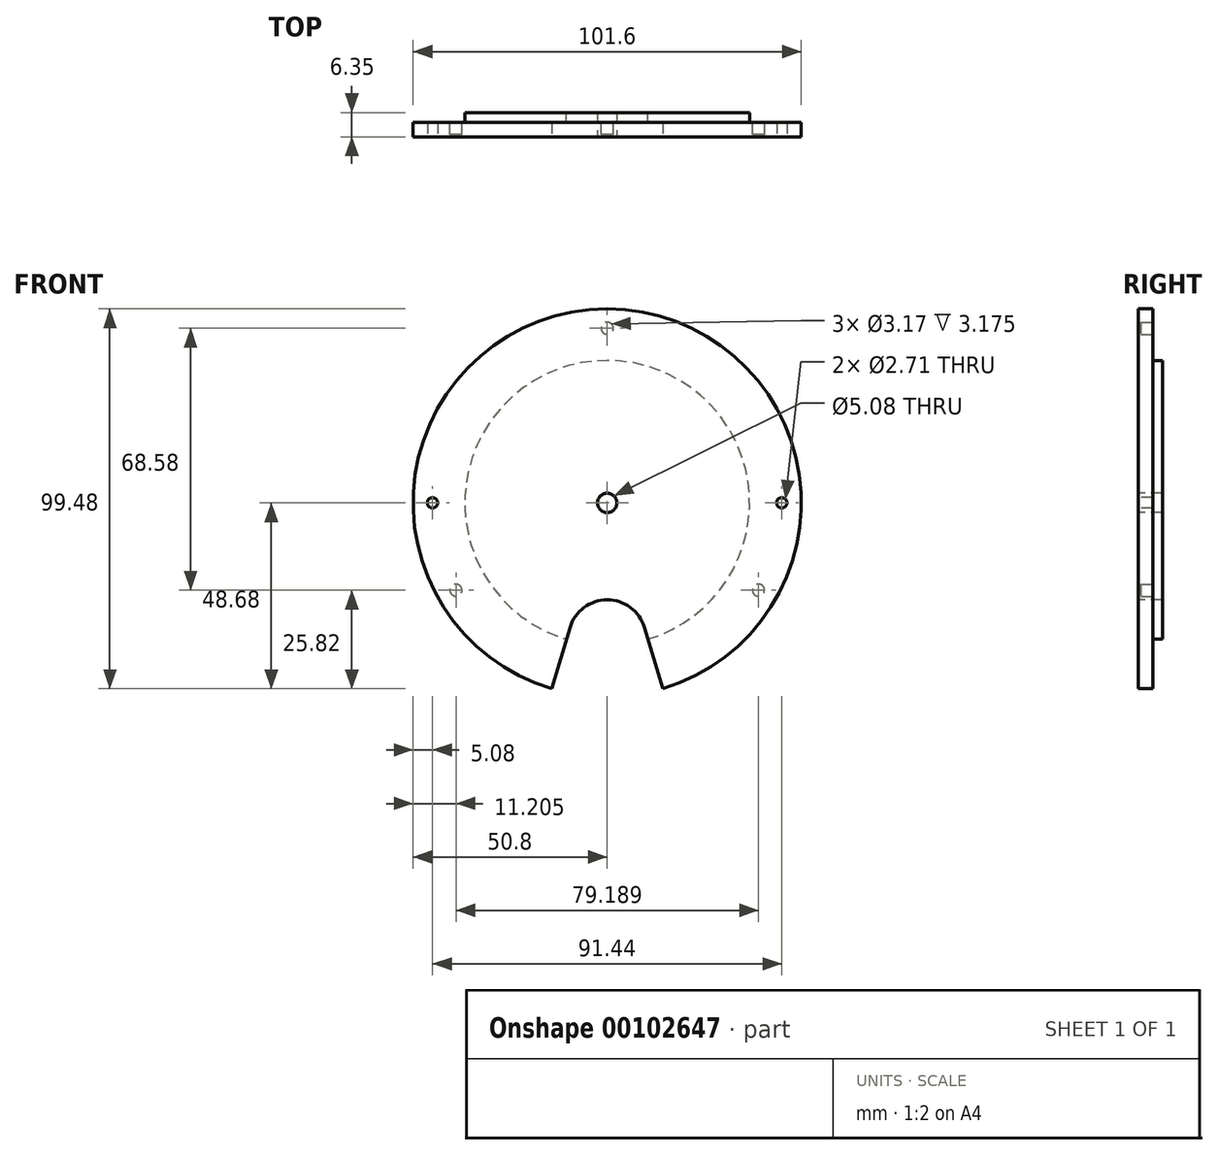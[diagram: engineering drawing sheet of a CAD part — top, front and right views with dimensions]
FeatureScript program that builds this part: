
annotation { "Feature Type Name" : "Feature", "Feature Type Description" : "" }
export const myFeature = defineFeature(function(context is Context, id is Id, definition is map)
    precondition{}
    {
        {
            var Q0;
            Q0=qCreatedBy(makeId("Front.planeOp"),FACE);
            var sketch = newSketch(context, id + "F0", { "sketchPlane" : qUnion([Q0])});
            skCircle(sketch, "E0", {"center": v(0, 0) * mm, "radius": 50.8 * mm});
            skSolve(sketch);
        }
        {
            var Q0;
            Q0=makeQuery(id+"F0.imprint","IMPRINT",FACE,{"disambiguationData":[TD([[makeQuery(id+"F0.imprint","IMPRINT",EDGE,{"derivedFrom":sQuery(id+"F0.wireOp",EDGE,"E0")}),1.0]])]});
            extrude(context, id + "F1", {"entities" : qUnion([Q0]), "oppositeDirection" : true, "depth" : 6.35 * mm});
        }
        {
            var Q0;
            Q0=makeQuery(id+"F1.opExtrude","CAP_FACE",FACE,{"disambiguationData":[OSD([sQuery(id+"F0.wireOp",EDGE,"E0")])],"isStart":false});
            var sketch = newSketch(context, id + "F2", { "sketchPlane" : qUnion([Q0])});
            skCircle(sketch, "E1", {"center": v(0, 0) * mm, "radius": 37.27 * mm});
            skSolve(sketch);
        }
        {
            var Q0;
            Q0=makeQuery(id+"F2.imprint","IMPRINT",FACE,{"disambiguationData":[TD([[makeQuery(id+"F2.imprint","IMPRINT",EDGE,{"derivedFrom":sQuery(id+"F2.wireOp",EDGE,"E1")}),-1.0]])]});
            extrude(context, id + "F3", {"entities" : qUnion([Q0]), "operationType" : NewBodyOperationType.REMOVE, "oppositeDirection" : true, "depth" : 2.54 * mm});
        }
        {
            var Q0;
            Q0=makeQuery(id+"F1.opExtrude","CAP_FACE",FACE,{"disambiguationData":[OSD([sQuery(id+"F0.wireOp",EDGE,"E0")])],"isStart":true});
            var sketch = newSketch(context, id + "F4", { "sketchPlane" : qUnion([Q0])});
            skCircle(sketch, "E2", {"center": v(0, 0) * mm, "radius": 2.54 * mm});
            skLineSegment(sketch, "E3", {"start": v(0, 63.69) * mm, "end": v(0, -59.89) * mm, "construction": true});
            skLineSegment(sketch, "E4", {"start": v(-63.21, 0) * mm, "end": v(63.78, 0) * mm, "construction": true});
            skCircle(sketch, "E5", {"center": v(-45.72, 0) * mm, "radius": 1.35 * mm});
            skCircle(sketch, "E6", {"center": v(45.72, 0) * mm, "radius": 1.35 * mm});
            skSolve(sketch);
        }
        {
            var Q0;
            Q0=makeQuery(id+"F4.imprint","IMPRINT",FACE,{"disambiguationData":[TD([[makeQuery(id+"F4.imprint","IMPRINT",EDGE,{"derivedFrom":sQuery(id+"F4.wireOp",EDGE,"E2")}),1.0]])]});
            var Q1;
            Q1=makeQuery(id+"F4.imprint","IMPRINT",FACE,{"disambiguationData":[TD([[makeQuery(id+"F4.imprint","IMPRINT",EDGE,{"derivedFrom":sQuery(id+"F4.wireOp",EDGE,"E5")}),1.0]])]});
            var Q2;
            Q2=makeQuery(id+"F4.imprint","IMPRINT",FACE,{"disambiguationData":[TD([[makeQuery(id+"F4.imprint","IMPRINT",EDGE,{"derivedFrom":sQuery(id+"F4.wireOp",EDGE,"E6")}),1.0]])]});
            extrude(context, id + "F5", {"entities" : qUnion([Q0, Q1, Q2]), "operationType" : NewBodyOperationType.REMOVE, "endBound" : BoundingType.THROUGH_ALL, "oppositeDirection" : true, "depth" : 25 * mm});
        }
        {
            var Q0;
            Q0=makeQuery(id+"F1.opExtrude","CAP_FACE",FACE,{"disambiguationData":[OSD([sQuery(id+"F0.wireOp",EDGE,"E0")])],"isStart":true});
            var sketch = newSketch(context, id + "F6", { "sketchPlane" : qUnion([Q0])});
            skLineSegment(sketch, "E7", {"start": v(0, 39.75) * mm, "end": v(0, -44.83) * mm, "construction": true});
            skCircle(sketch, "E8", {"center": v(0, 0) * mm, "radius": 25.4 * mm, "construction": true});
            skCircle(sketch, "E9", {"center": v(0, -35.56) * mm, "radius": 10.16 * mm, "construction": true});
            skPoint(sketch, "E9.first.point", {"position": v(0, -25.4) * mm});
            skPoint(sketch, "E9.second.point", {"position": v(-10.15, -35.13) * mm});
            skPoint(sketch, "E9.third.point", {"position": v(10.15, -35.2) * mm});
            skLineSegment(sketch, "E10", {"start": v(0, 0) * mm, "end": v(-14.51, -48.68) * mm, "construction": true});
            skLineSegment(sketch, "E11", {"start": v(0, 0) * mm, "end": v(14.51, -48.68) * mm, "construction": true});
            skLineSegment(sketch, "E12", {"start": v(-9.74, -32.66) * mm, "end": v(-14.51, -48.68) * mm});
            skLineSegment(sketch, "E13", {"start": v(9.74, -32.66) * mm, "end": v(14.51, -48.68) * mm});
            skArc(sketch, "E14", {"start": v(-9.74, -32.66) * mm, "mid": v(0, -25.4) * mm, "end": v(9.74, -32.66) * mm});
            skSolve(sketch);
        }
        {
            var Q0;
            Q0 = qSketchRegion(id + "F6", true);
            var Q1;
            {var subQ0=sQuery(id+"F6.wireOp",EDGE,"E12");Q1=makeQuery(id+"F6.imprint","IMPRINT",FACE,{"disambiguationData":[TD([[makeQuery(id+"F6.imprint","IMPRINT",EDGE,{"derivedFrom":subQ0}),1.0]])]});}
            extrude(context, id + "F7", {"entities" : qUnion([Q0, Q1]), "operationType" : NewBodyOperationType.REMOVE, "endBound" : BoundingType.THROUGH_ALL, "oppositeDirection" : true, "depth" : 25 * mm});
        }
        {
            var Q0;
            Q0=makeQuery(id+"F3.boolean.opBoolean","COPY",FACE,{"derivedFrom":makeQuery(id+"F3.opExtrude","CAP_FACE",FACE,{"disambiguationData":[OSD([sQuery(id+"F0.wireOp",EDGE,"E0"),sQuery(id+"F2.wireOp",EDGE,"E1")])],"isStart":false})});
            var sketch = newSketch(context, id + "F8", { "sketchPlane" : qUnion([Q0])});
            skCircle(sketch, "E15", {"center": v(0, 0) * mm, "radius": 45.72 * mm, "construction": true});
            skLineSegment(sketch, "E16", {"start": v(0, 0) * mm, "end": v(0, 52.86) * mm, "construction": true});
            skLineSegment(sketch, "E17", {"start": v(0, 0) * mm, "end": v(-52.85, -30.51) * mm, "construction": true});
            skLineSegment(sketch, "E18", {"start": v(0, 0) * mm, "end": v(48.48, -27.99) * mm, "construction": true});
            skCircle(sketch, "E19", {"center": v(-39.6, -22.86) * mm, "radius": 1.59 * mm});
            skCircle(sketch, "E20", {"center": v(0, 45.72) * mm, "radius": 1.59 * mm});
            skCircle(sketch, "E21", {"center": v(39.6, -22.86) * mm, "radius": 1.59 * mm});
            skSolve(sketch);
        }
        {
            var Q0;
            Q0=makeQuery(id+"F8.imprint","IMPRINT",FACE,{"disambiguationData":[TD([[makeQuery(id+"F8.imprint","IMPRINT",EDGE,{"derivedFrom":sQuery(id+"F8.wireOp",EDGE,"E20")}),1.0]])]});
            var Q1;
            Q1=makeQuery(id+"F8.imprint","IMPRINT",FACE,{"disambiguationData":[TD([[makeQuery(id+"F8.imprint","IMPRINT",EDGE,{"derivedFrom":sQuery(id+"F8.wireOp",EDGE,"E21")}),1.0]])]});
            var Q2;
            Q2=makeQuery(id+"F8.imprint","IMPRINT",FACE,{"disambiguationData":[TD([[makeQuery(id+"F8.imprint","IMPRINT",EDGE,{"derivedFrom":sQuery(id+"F8.wireOp",EDGE,"E19")}),1.0]])]});
            extrude(context, id + "F9", {"entities" : qUnion([Q0, Q1, Q2]), "operationType" : NewBodyOperationType.REMOVE, "oppositeDirection" : true, "depth" : 3.17 * mm});
        }
    });
